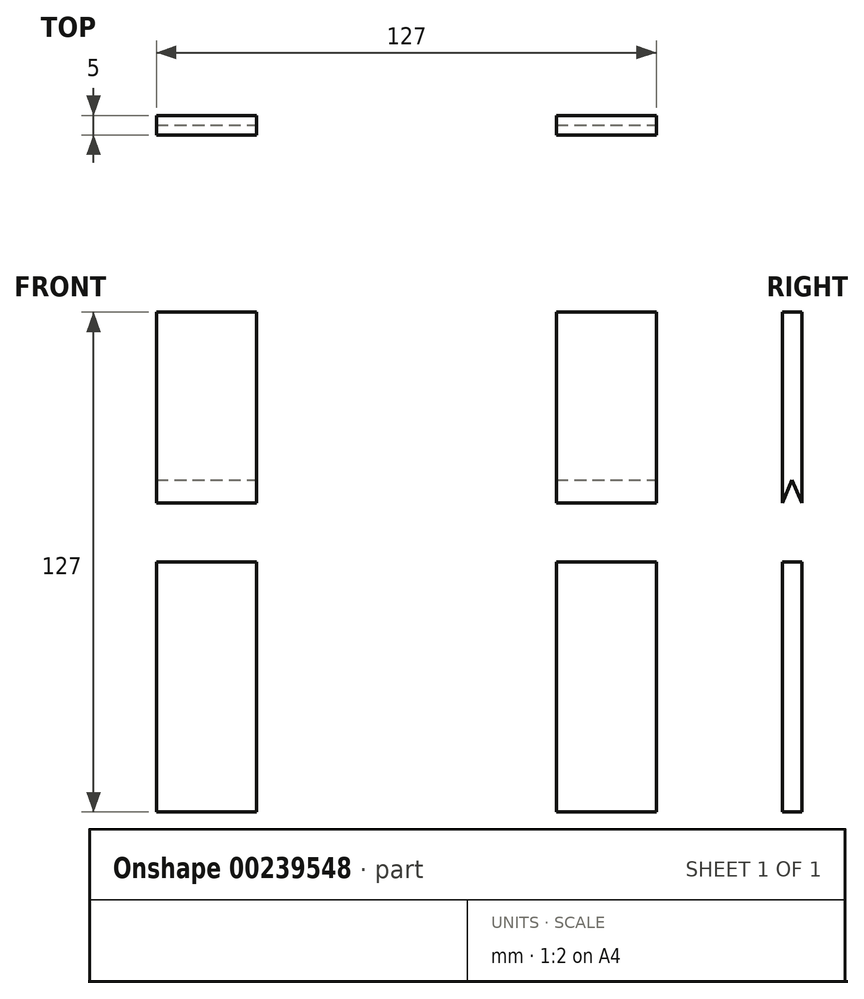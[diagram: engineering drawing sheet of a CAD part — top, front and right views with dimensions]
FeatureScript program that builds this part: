
annotation { "Feature Type Name" : "Feature", "Feature Type Description" : "" }
export const myFeature = defineFeature(function(context is Context, id is Id, definition is map)
    precondition{}
    {
        {
            assignVariable(context, id + "F0", {"name" : "L", "anyValue" : 5});
        }
        {
            var Q0;
            Q0=qCreatedBy(makeId("Front.planeOp"),FACE);
            var sketch = newSketch(context, id + "F1", { "sketchPlane" : qUnion([Q0])});
            skLineSegment(sketch, "E0.bottom", {"start": v(-63.5, -63.5) * mm, "end": v(63.5, -63.5) * mm});
            skLineSegment(sketch, "E0.top", {"start": v(-63.5, 63.5) * mm, "end": v(63.5, 63.5) * mm});
            skLineSegment(sketch, "E0.left", {"start": v(-63.5, -63.5) * mm, "end": v(-63.5, 63.5) * mm});
            skLineSegment(sketch, "E0.right", {"start": v(63.5, -63.5) * mm, "end": v(63.5, 63.5) * mm});
            skPoint(sketch, "E0.middle", {"position": v(0, 0) * mm});
            skSolve(sketch);
        }
        {
            var Q0;
            Q0 = qSketchRegion(id + "F1", true);
            extrude(context, id + "F2", {"entities" : qUnion([Q0]), "endBound" : BoundingType.SYMMETRIC, "depth" : (getVariable(context, 'L')) * mm});
        }
        {
            var Q0;
            Q0=makeQuery(id+"F2.opExtrude","SWEPT_FACE",FACE,{"disambiguationData":[OSD([sQuery(id+"F1.wireOp",EDGE,"E0.bottom")])]});
            var sketch = newSketch(context, id + "F3", { "sketchPlane" : qUnion([Q0])});
            skLineSegment(sketch, "E1.bottom", {"start": v(38.1, -38.1) * mm, "end": v(-38.1, -38.1) * mm});
            skLineSegment(sketch, "E1.top", {"start": v(38.1, 38.1) * mm, "end": v(-38.1, 38.1) * mm});
            skLineSegment(sketch, "E1.left", {"start": v(-38.1, -38.1) * mm, "end": v(-38.1, 38.1) * mm});
            skLineSegment(sketch, "E1.right", {"start": v(38.1, -38.1) * mm, "end": v(38.1, 38.1) * mm});
            skPoint(sketch, "E1.middle", {"position": v(0, 0) * mm});
            skSolve(sketch);
        }
        {
            var Q0;
            Q0 = qSketchRegion(id + "F3", true);
            extrude(context, id + "F4", {"entities" : qUnion([Q0]), "operationType" : NewBodyOperationType.REMOVE, "oppositeDirection" : true, "depth" : 135.64 * mm});
        }
        {
            var Q0;
            Q0=makeQuery(id+"F2.opExtrude","SWEPT_FACE",FACE,{"disambiguationData":[OSD([sQuery(id+"F1.wireOp",EDGE,"E0.right")])]});
            var sketch = newSketch(context, id + "F5", { "sketchPlane" : qUnion([Q0])});
            skLineSegment(sketch, "E2", {"start": v(0, 20.92) * mm, "end": v(-8.9, 0) * mm});
            skLineSegment(sketch, "E3", {"start": v(-8.9, 0) * mm, "end": v(8.9, 0) * mm});
            skLineSegment(sketch, "E4", {"start": v(8.9, 0) * mm, "end": v(0, 20.92) * mm});
            skSolve(sketch);
        }
        {
            var Q0;
            Q0 = qSketchRegion(id + "F5", true);
            extrude(context, id + "F6", {"entities" : qUnion([Q0]), "operationType" : NewBodyOperationType.REMOVE, "oppositeDirection" : true, "depth" : 146.3 * mm});
        }
        {
            var Q0;
            Q0=makeQuery(id+"F2.opExtrude","CAP_FACE",FACE,{"disambiguationData":[OSD([sQuery(id+"F1.wireOp",EDGE,"E0.bottom"),sQuery(id+"F1.wireOp",EDGE,"E0.top"),sQuery(id+"F1.wireOp",EDGE,"E0.left"),sQuery(id+"F1.wireOp",EDGE,"E0.right")])],"isStart":true});
            var sketch = newSketch(context, id + "F7", { "sketchPlane" : qUnion([Q0])});
            skCircle(sketch, "E5", {"center": v(0, 0) * mm, "radius": 25.4 * mm});
            skSolve(sketch);
        }
        {
            var Q0;
            Q0 = qSketchRegion(id + "F7", true);
            extrude(context, id + "F8", {"entities" : qUnion([Q0]), "operationType" : NewBodyOperationType.REMOVE, "oppositeDirection" : true, "depth" : 142 * mm});
        }
    });
